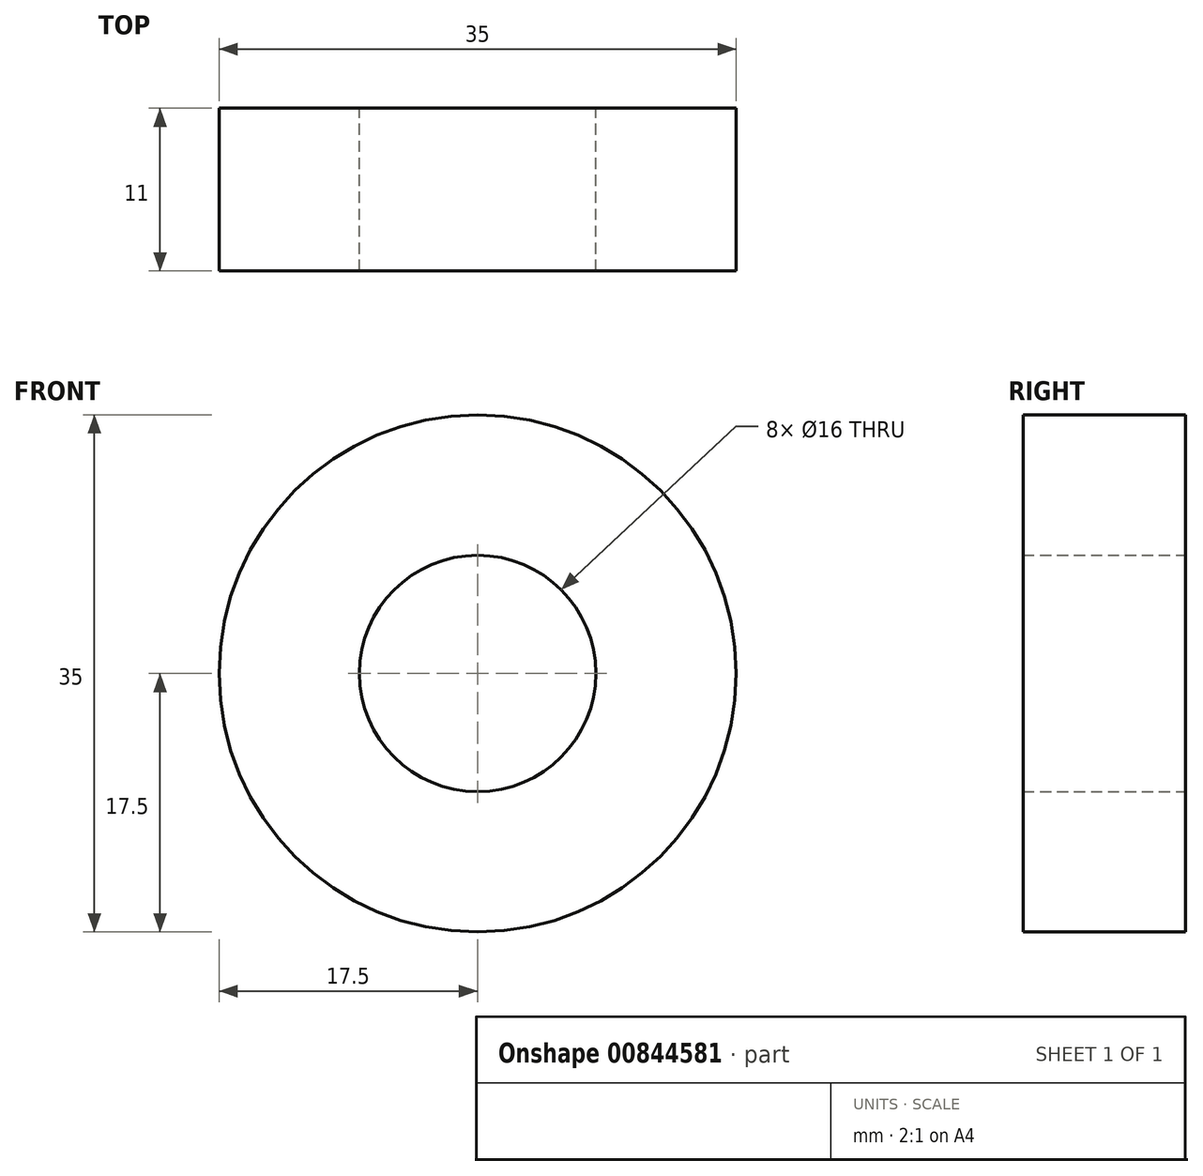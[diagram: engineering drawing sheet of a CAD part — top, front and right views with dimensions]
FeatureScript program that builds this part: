
annotation { "Feature Type Name" : "Feature", "Feature Type Description" : "" }
export const myFeature = defineFeature(function(context is Context, id is Id, definition is map)
    precondition{}
    {
        {
            var Q0;
            Q0=qCreatedBy(makeId("Front.planeOp"),FACE);
            var sketch = newSketch(context, id + "F0", { "sketchPlane" : qUnion([Q0])});
            skCircle(sketch, "E0", {"center": v(0, 0) * mm, "radius": 8 * mm});
            skCircle(sketch, "E1", {"center": v(0, 0) * mm, "radius": 17.5 * mm});
            skSolve(sketch);
        }
        {
            var Q0;
            Q0=makeQuery(id+"F0.imprint","IMPRINT",FACE,{"disambiguationData":[TD([[makeQuery(id+"F0.imprint","IMPRINT",EDGE,{"derivedFrom":sQuery(id+"F0.wireOp",EDGE,"E0")}),-1.0]])]});
            extrude(context, id + "F1", {"entities" : qUnion([Q0]), "depth" : 11 * mm, "offsetDistance" : 25 * mm});
        }
    });
